# Revit family: 1Electronics_Commercial-Loudspeakers_Biamp_Outdoor-Loudspeaker_ROCK608
name_source: partatom
category: Communication Devices
units: mm (PartAtom-declared; Revit-internal decimal feet)

## family parameters
Cut with Voids When Loaded = No
Host = Face
Maintain Annotation Orientation = No
OmniClass Number = 23.85.10.11.14.14.14
OmniClass Title = Loudspeakers
Part Type = Normal
Room Calculation Point = No
Round Connector Dimension = Use Diameter
Shared = No

## types (1)
- ROCK608
    Connector Description = Spring terminals; 8 Ω Low Impedance, 70/100V
    Default Elevation = 0 "
    Depth = 11.02 "
    Description = ROCK608 Rock Design Outdoor Loudspeaker
    Frequency response in Hz = 60-20k
    Grill Material = Biamp - Plastic - Gray(Grid)
    Height = 10.24 "
    Horizontal dispersion angle 1000 Hz = 180°
    Housing Material = Biamp - Plastic - Gray
    Impedance (ohms) = 8
    Loudspeaker system = 2-way
    Low impedance RMS power in watts = 25
    Low impedance dynamic power in watts = 60
    Manufacturer = Biamp
    Max SPL 1m in dB = 105
    Model = ROCK608
    Product Documentation Link = https://downloads.biamp.com
    Product Page URL = https://www.biamp.com
    Product data url = https://bimobject.com
    SPL 1W/1m in dB = 92
    Tweeter size in inch = 1
    URL = https://www.biamp.com
    Vertical dispersion angle 1000 Hz = 55°
    Weight = 7.95 lbf
    Width = 7.87 "
    Woofer cone material = Polypropylene
    Woofer size in inch = 6.5

## geometry (parser evidence)
native form markers: Sweep x2
no freeform markers — native parametric forms only
